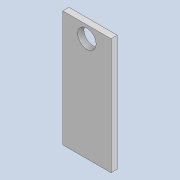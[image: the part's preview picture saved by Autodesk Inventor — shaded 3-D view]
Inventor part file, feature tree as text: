
AUTODESK INVENTOR PART (.ipt)
format: ipt  version: 2021 (Build 250183000, 183)  size: 87,040 bytes
history: native  units: mm
features: extrude x2, sketch x2, other x1
ambient origin geometry x8: Origin, YZ Plane, XZ Plane, XY Plane, X Axis, Y Axis, Z Axis, Center Point
bodies: Body1 (feature_tree)
feature tree (5):
  other  "Sólido1"
  extrude  "Extrusión1"  Depth=120.0mm
  extrude  "Extrusión2"  Depth=9.5mm
  sketch  "Boceto1"  dims[d0=50.0mm d1=120.0mm]
  sketch  "Boceto2"  dims[d2=6.4mm d3=0.0mm d4=3.0mm d5=9.5mm d6=19.0mm d7=0.0mm d8=0.0mm]
